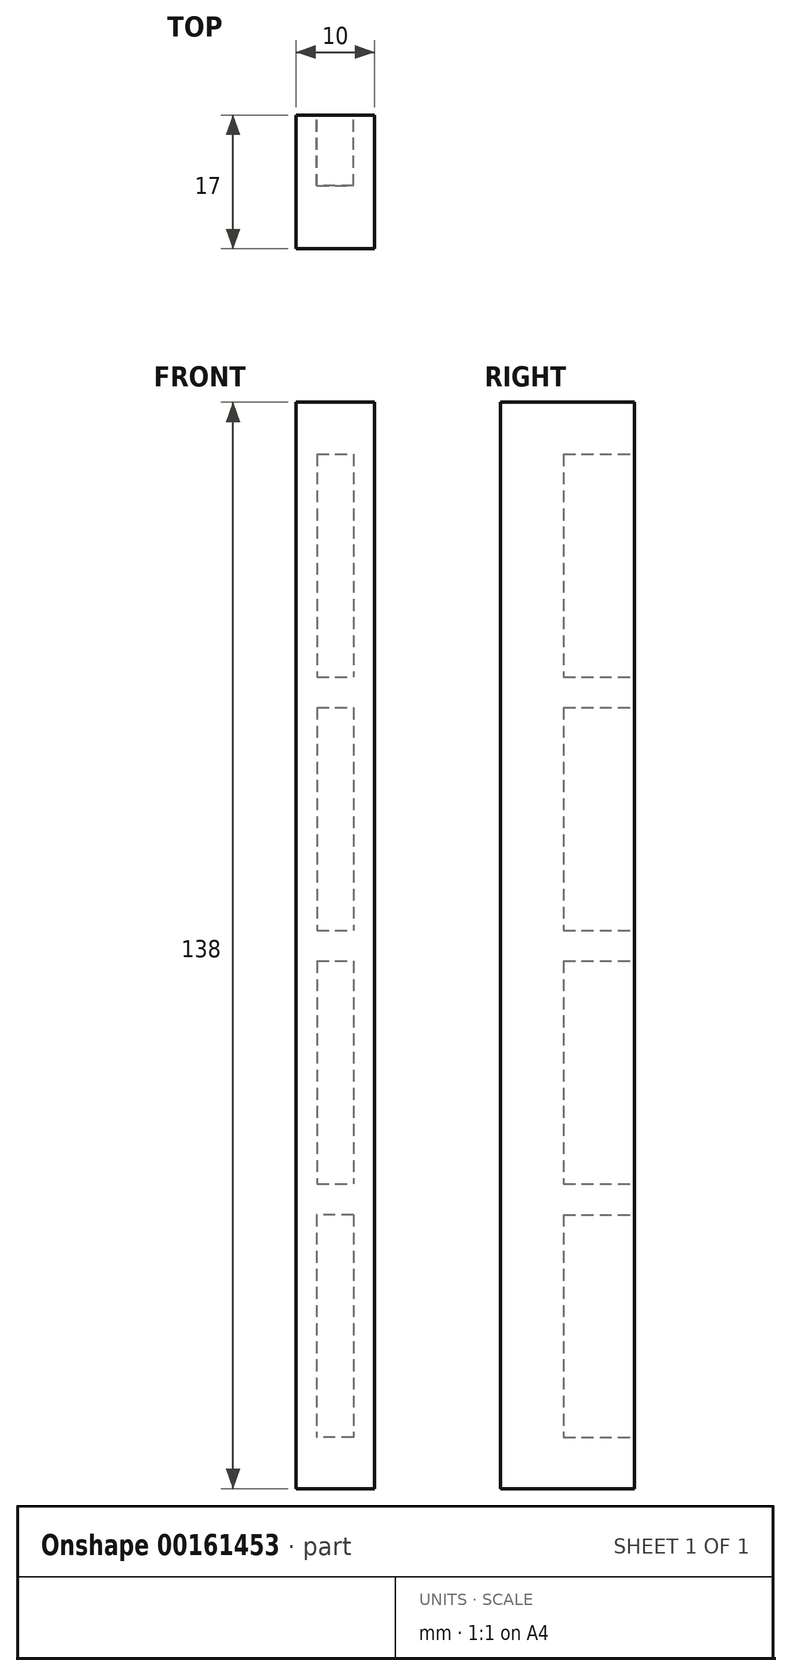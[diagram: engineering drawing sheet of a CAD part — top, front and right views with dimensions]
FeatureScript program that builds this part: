
annotation { "Feature Type Name" : "Feature", "Feature Type Description" : "" }
export const myFeature = defineFeature(function(context is Context, id is Id, definition is map)
    precondition{}
    {
        {
            var Q0;
            Q0=qCreatedBy(makeId("Front.planeOp"),FACE);
            var sketch = newSketch(context, id + "F0", { "sketchPlane" : qUnion([Q0])});
            skLineSegment(sketch, "E0.bottom", {"start": v(-30.25, 56.68) * mm, "end": v(-20.25, 56.68) * mm});
            skLineSegment(sketch, "E0.top", {"start": v(-30.25, -81.32) * mm, "end": v(-20.25, -81.32) * mm});
            skLineSegment(sketch, "E0.left", {"start": v(-30.25, 56.68) * mm, "end": v(-30.25, -81.32) * mm});
            skLineSegment(sketch, "E0.right", {"start": v(-20.25, 56.68) * mm, "end": v(-20.25, -81.32) * mm});
            skLineSegment(sketch, "E1.bottom", {"start": v(-27.56, 50.08) * mm, "end": v(-22.96, 50.08) * mm});
            skLineSegment(sketch, "E1.top", {"start": v(-27.56, 21.78) * mm, "end": v(-22.96, 21.78) * mm});
            skLineSegment(sketch, "E1.left", {"start": v(-27.56, 50.08) * mm, "end": v(-27.56, 21.78) * mm});
            skLineSegment(sketch, "E1.right", {"start": v(-22.96, 50.08) * mm, "end": v(-22.96, 21.78) * mm});
            skLineSegment(sketch, "E2", {"start": v(-26.53, 56.68) * mm, "end": v(-26.53, 50.08) * mm, "construction": true});
            skLineSegment(sketch, "E3", {"start": v(-27.56, 45.9) * mm, "end": v(-30.25, 45.9) * mm, "construction": true});
            skLineSegment(sketch, "E4", {"start": v(-22.96, 46.31) * mm, "end": v(-20.25, 46.31) * mm, "construction": true});
            skLineSegment(sketch, "E5", {"start": v(-25.26, 21.78) * mm, "end": v(-25.26, 17.88) * mm, "construction": true});
            skLineSegment(sketch, "E6", {"start": v(-27.56, 21.78) * mm, "end": v(-27.56, 17.88) * mm, "construction": true});
            skLineSegment(sketch, "E7", {"start": v(-22.96, 21.78) * mm, "end": v(-22.96, 17.88) * mm, "construction": true});
            skLineSegment(sketch, "E8.bottom", {"start": v(-27.56, 17.88) * mm, "end": v(-22.96, 17.88) * mm});
            skLineSegment(sketch, "E8.top", {"start": v(-27.56, -10.42) * mm, "end": v(-22.96, -10.42) * mm});
            skLineSegment(sketch, "E8.left", {"start": v(-27.56, 17.88) * mm, "end": v(-27.56, -10.42) * mm});
            skLineSegment(sketch, "E8.right", {"start": v(-22.96, 17.88) * mm, "end": v(-22.96, -10.42) * mm});
            skLineSegment(sketch, "E9", {"start": v(-22.96, -10.42) * mm, "end": v(-22.96, -14.32) * mm, "construction": true});
            skLineSegment(sketch, "E10", {"start": v(-27.56, -10.42) * mm, "end": v(-27.56, -14.32) * mm, "construction": true});
            skLineSegment(sketch, "E11.bottom", {"start": v(-27.56, -14.32) * mm, "end": v(-22.96, -14.32) * mm});
            skLineSegment(sketch, "E11.top", {"start": v(-27.56, -42.62) * mm, "end": v(-22.96, -42.62) * mm});
            skLineSegment(sketch, "E11.left", {"start": v(-27.56, -14.32) * mm, "end": v(-27.56, -42.62) * mm});
            skLineSegment(sketch, "E11.right", {"start": v(-22.96, -14.32) * mm, "end": v(-22.96, -42.62) * mm});
            skLineSegment(sketch, "E12", {"start": v(-27.56, -41.18) * mm, "end": v(-27.56, -42.62) * mm});
            skLineSegment(sketch, "E13", {"start": v(-22.96, -42.62) * mm, "end": v(-22.96, -46.52) * mm, "construction": true});
            skLineSegment(sketch, "E14.bottom", {"start": v(-22.96, -46.52) * mm, "end": v(-27.62, -46.52) * mm});
            skLineSegment(sketch, "E14.top", {"start": v(-22.96, -74.82) * mm, "end": v(-27.62, -74.82) * mm});
            skLineSegment(sketch, "E14.left", {"start": v(-22.96, -46.52) * mm, "end": v(-22.96, -74.82) * mm});
            skLineSegment(sketch, "E14.right", {"start": v(-27.62, -46.52) * mm, "end": v(-27.62, -74.82) * mm});
            skLineSegment(sketch, "E15", {"start": v(-22.96, -74.82) * mm, "end": v(-22.96, -81.32) * mm, "construction": true});
            skSolve(sketch);
        }
        {
            var Q0;
            Q0=makeQuery(id+"F0.imprint","IMPRINT",FACE,{"disambiguationData":[TD([[makeQuery(id+"F0.imprint","IMPRINT",EDGE,{"derivedFrom":sQuery(id+"F0.wireOp",EDGE,"E0.bottom")}),-1.0]])]});
            var Q1;
            Q1=makeQuery(id+"F0.imprint","IMPRINT",FACE,{"disambiguationData":[TD([[makeQuery(id+"F0.imprint","IMPRINT",EDGE,{"derivedFrom":sQuery(id+"F0.wireOp",EDGE,"E1.bottom")}),-1.0]])]});
            var Q2;
            Q2=makeQuery(id+"F0.imprint","IMPRINT",FACE,{"disambiguationData":[TD([[makeQuery(id+"F0.imprint","IMPRINT",EDGE,{"derivedFrom":sQuery(id+"F0.wireOp",EDGE,"E8.bottom")}),-1.0]])]});
            var Q3;
            Q3=makeQuery(id+"F0.imprint","IMPRINT",FACE,{"disambiguationData":[TD([[makeQuery(id+"F0.imprint","IMPRINT",EDGE,{"derivedFrom":sQuery(id+"F0.wireOp",EDGE,"E11.bottom")}),-1.0]])]});
            var Q4;
            Q4=makeQuery(id+"F0.imprint","IMPRINT",FACE,{"disambiguationData":[TD([[makeQuery(id+"F0.imprint","IMPRINT",EDGE,{"derivedFrom":sQuery(id+"F0.wireOp",EDGE,"E14.bottom")}),1.0]])]});
            extrude(context, id + "F1", {"entities" : qUnion([Q0, Q1, Q2, Q3, Q4]), "depth" : 17 * mm});
        }
        {
            var Q0;
            Q0=makeQuery(id+"F0.imprint","IMPRINT",FACE,{"disambiguationData":[TD([[makeQuery(id+"F0.imprint","IMPRINT",EDGE,{"derivedFrom":sQuery(id+"F0.wireOp",EDGE,"E1.bottom")}),-1.0]])]});
            var Q1;
            Q1=makeQuery(id+"F0.imprint","IMPRINT",FACE,{"disambiguationData":[TD([[makeQuery(id+"F0.imprint","IMPRINT",EDGE,{"derivedFrom":sQuery(id+"F0.wireOp",EDGE,"E8.bottom")}),-1.0]])]});
            var Q2;
            Q2=makeQuery(id+"F0.imprint","IMPRINT",FACE,{"disambiguationData":[TD([[makeQuery(id+"F0.imprint","IMPRINT",EDGE,{"derivedFrom":sQuery(id+"F0.wireOp",EDGE,"E11.bottom")}),-1.0]])]});
            var Q3;
            Q3=makeQuery(id+"F0.imprint","IMPRINT",FACE,{"disambiguationData":[TD([[makeQuery(id+"F0.imprint","IMPRINT",EDGE,{"derivedFrom":sQuery(id+"F0.wireOp",EDGE,"E14.bottom")}),1.0]])]});
            extrude(context, id + "F2", {"entities" : qUnion([Q0, Q1, Q2, Q3]), "operationType" : NewBodyOperationType.REMOVE, "depth" : 9 * mm});
        }
    });
